# Revit family: Faucet-Two_Handle-American_Standard-Heritage-7298_Series
name_source: partatom
category: Plumbing Fixtures
revit_build: Autodesk Revit 2015 (Build: 20140606_1530(x64)
units: mm (PartAtom-declared; Revit-internal decimal feet)

## types (3) — shared parameters
ADA Compliant = Yes
Assembly Code = D2020300
CW Connection = Yes
CWFU = 1.5
Cold Water Connection Diameter = 0' - 0 1/2"
Description = Heritage Two-Handle Wall-Mounted Sink Faucet With Brass Spout.
Finish = Brass-American Standard-002-Polished Chrome
HW Connection = Yes
HWFU = 1.5
Hot Water Connection Diameter = 0' - 0 1/2"
Length = 0' - 8"
Manufacturer = American Standard
Material = Metal-American Standard-002-Polished Chrome
Product Documentation Link = https://www.americanstandard-us.com
Product URL = https://www.americanstandard-us.com
URL = http://www.americanstandard-us.com
Vent Connection = No
Waste Connection = No
Width = 0' - 2 3/4"
zero-valued in all types: WFU

## per-type parameters (varying)
| type | Brass Lever Handles | Default Elevation | Flow Rate | Height | Porcelain Lever Handles | Specification |
| 7298.152 | Yes | 3' - 0" | 1.5gmp/5.7L/min. | 0' - 7" | No | Wall-Mount Sink Faucet. 8" tubular swivel spout. Brass Lever Handles. Less soap dish. |
| 7298.252 | No | 0' - 0" | 2.2gmp/8.3L/min. | 0' - 7 3/8" | Yes | Wall-Mount Sink Faucet. 8" tubular swivel spout. Porcelain Lever Handles. |
| 7298.252.F15 | No | 0' - 0" | 1.5gmp/5.7L/min. | 0' - 7 3/8" | Yes | Wall-Mount Sink Faucet. 8" tubular swivel spout. Porcelain Lever Handles. |

note: column(s) folded — value = type name in every type: Model

## geometry (parser evidence)
native form markers: Sweep x2
no freeform markers — native parametric forms only
